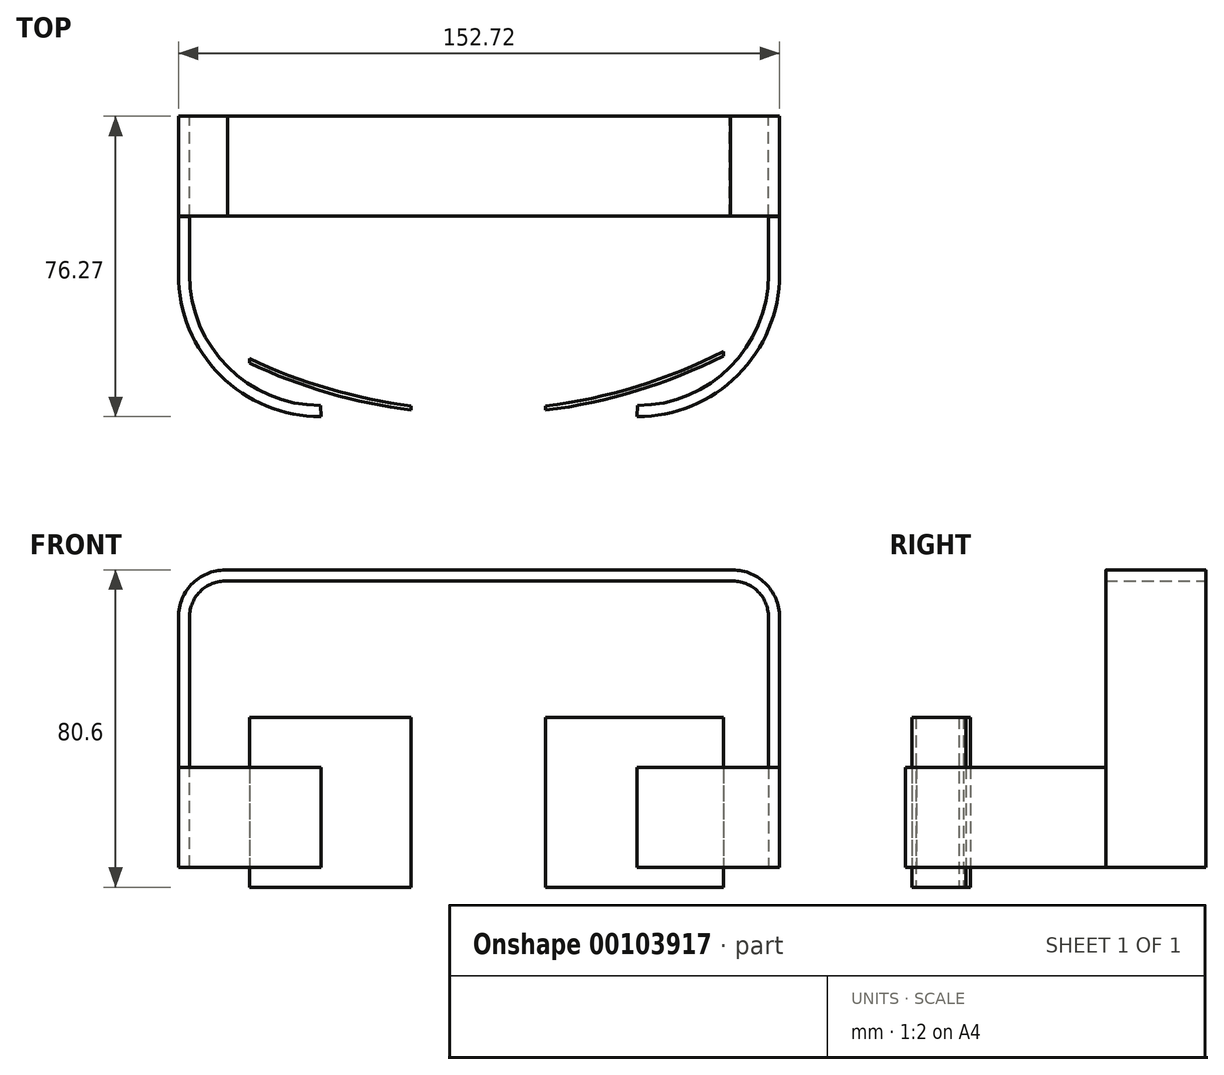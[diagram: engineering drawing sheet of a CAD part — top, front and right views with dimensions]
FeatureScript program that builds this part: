
annotation { "Feature Type Name" : "Feature", "Feature Type Description" : "" }
export const myFeature = defineFeature(function(context is Context, id is Id, definition is map)
    precondition{}
    {
        {
            var Q0;
            Q0=qCreatedBy(makeId("Front.planeOp"),FACE);
            var sketch = newSketch(context, id + "F0", { "sketchPlane" : qUnion([Q0])});
            skLineSegment(sketch, "E0", {"start": v(-76.36, 0) * mm, "end": v(-76.36, 63.57) * mm});
            skArc(sketch, "E1", {"start": v(-63.85, 75.5) * mm, "mid": v(-72.66, 72.22) * mm, "end": v(-76.36, 63.57) * mm});
            skLineSegment(sketch, "E2", {"start": v(-63.85, 75.5) * mm, "end": v(63.85, 75.5) * mm});
            skLineSegment(sketch, "E3", {"start": v(76.36, 0) * mm, "end": v(76.36, 63.57) * mm});
            skArc(sketch, "E4", {"start": v(76.36, 63.57) * mm, "mid": v(72.66, 72.22) * mm, "end": v(63.85, 75.5) * mm});
            skLineSegment(sketch, "E5", {"start": v(-73.55, 0) * mm, "end": v(-73.55, 63.57) * mm});
            skArc(sketch, "E6", {"start": v(-73.55, 63.57) * mm, "mid": v(-70.57, 70.32) * mm, "end": v(-63.58, 72.68) * mm});
            skLineSegment(sketch, "E7", {"start": v(-63.58, 72.68) * mm, "end": v(63.58, 72.68) * mm});
            skLineSegment(sketch, "E8", {"start": v(73.55, 0) * mm, "end": v(73.55, 63.57) * mm});
            skArc(sketch, "E9", {"start": v(73.55, 63.57) * mm, "mid": v(70.57, 70.32) * mm, "end": v(63.58, 72.68) * mm});
            skLineSegment(sketch, "E10", {"start": v(-76.36, 0) * mm, "end": v(-73.55, 0) * mm});
            skLineSegment(sketch, "E11", {"start": v(73.55, 0) * mm, "end": v(76.36, 0) * mm});
            skSolve(sketch);
        }
        {
            var Q0;
            Q0=qCreatedBy(makeId("Top.planeOp"),FACE);
            var sketch = newSketch(context, id + "F1", { "sketchPlane" : qUnion([Q0])});
            skLineSegment(sketch, "E12", {"start": v(73.55, -25.42) * mm, "end": v(73.55, -40.22) * mm});
            skLineSegment(sketch, "E13", {"start": v(76.36, -25.42) * mm, "end": v(76.36, -40.22) * mm});
            skLineSegment(sketch, "E14", {"start": v(-76.36, -25.42) * mm, "end": v(-76.36, -40.22) * mm});
            skLineSegment(sketch, "E15", {"start": v(-73.55, -25.42) * mm, "end": v(-73.55, -40.22) * mm});
            skArc(sketch, "E16", {"start": v(-73.55, -40.22) * mm, "mid": v(-63.81, -63.73) * mm, "end": v(-40.3, -73.46) * mm});
            skArc(sketch, "E17", {"start": v(-76.36, -40.22) * mm, "mid": v(-65.76, -65.75) * mm, "end": v(-40.2, -76.27) * mm});
            skArc(sketch, "E18", {"start": v(76.36, -40.22) * mm, "mid": v(65.76, -65.75) * mm, "end": v(40.2, -76.27) * mm});
            skArc(sketch, "E19", {"start": v(73.55, -40.22) * mm, "mid": v(63.81, -63.73) * mm, "end": v(40.3, -73.46) * mm});
            skLineSegment(sketch, "E20", {"start": v(-73.55, -25.42) * mm, "end": v(-76.36, -25.42) * mm});
            skLineSegment(sketch, "E21", {"start": v(-40.3, -73.46) * mm, "end": v(-40.2, -76.27) * mm});
            skLineSegment(sketch, "E22", {"start": v(40.2, -76.27) * mm, "end": v(40.3, -73.46) * mm});
            skLineSegment(sketch, "E23", {"start": v(73.55, -25.42) * mm, "end": v(76.36, -25.42) * mm});
            skSolve(sketch);
        }
        {
            var Q0;
            Q0 = qSketchRegion(id + "F0", true);
            extrude(context, id + "F2", {"entities" : qUnion([Q0]), "depth" : 25.4 * mm});
        }
        {
            var Q0;
            Q0=makeQuery(id+"F1.imprint","IMPRINT",FACE,{"disambiguationData":[TD([[makeQuery(id+"F1.imprint","IMPRINT",EDGE,{"derivedFrom":sQuery(id+"F1.wireOp",EDGE,"E12")}),1.0]])]});
            var Q1;
            Q1=makeQuery(id+"F1.imprint","IMPRINT",FACE,{"disambiguationData":[TD([[makeQuery(id+"F1.imprint","IMPRINT",EDGE,{"derivedFrom":sQuery(id+"F1.wireOp",EDGE,"E14")}),1.0]])]});
            var Q2;
            Q2=sQuery(id+"F1.wireOp",EDGE,"E20");
            var Q3;
            Q3=sQuery(id+"F1.wireOp",EDGE,"E15");
            var Q4;
            Q4=sQuery(id+"F1.wireOp",EDGE,"E14");
            var Q5;
            Q5=sQuery(id+"F1.wireOp",EDGE,"E17");
            var Q6;
            Q6=sQuery(id+"F1.wireOp",EDGE,"E16");
            var Q7;
            Q7=sQuery(id+"F1.wireOp",EDGE,"E21");
            var Q8;
            Q8=sQuery(id+"F1.wireOp",EDGE,"E12");
            var Q9;
            Q9=sQuery(id+"F1.wireOp",EDGE,"E13");
            var Q10;
            Q10=sQuery(id+"F1.wireOp",EDGE,"E23");
            var Q11;
            Q11=sQuery(id+"F1.wireOp",EDGE,"E18");
            var Q12;
            Q12=sQuery(id+"F1.wireOp",EDGE,"E19");
            var Q13;
            Q13=sQuery(id+"F1.wireOp",EDGE,"E22");
            extrude(context, id + "F3", {"entities" : qUnion([Q0, Q1]), "operationType" : NewBodyOperationType.ADD, "surfaceEntities" : qUnion([Q2, Q3, Q4, Q5, Q6, Q7, Q8, Q9, Q10, Q11, Q12, Q13]), "depth" : 25.4 * mm});
        }
        {
            var Q0;
            Q0=qCreatedBy(makeId("Top.planeOp"),FACE);
            var sketch = newSketch(context, id + "F4", { "sketchPlane" : qUnion([Q0])});
            skArc(sketch, "E24", {"start": v(-58.28, -62.73) * mm, "mid": v(-38.21, -70.3) * mm, "end": v(-17.21, -74.63) * mm});
            skArc(sketch, "E25", {"start": v(16.92, -74.67) * mm, "mid": v(40.1, -69.73) * mm, "end": v(62.1, -60.87) * mm});
            skArc(sketch, "E26", {"start": v(-58.28, -61.6) * mm, "mid": v(-38.22, -69.22) * mm, "end": v(-17.21, -73.6) * mm});
            skArc(sketch, "E27", {"start": v(16.92, -73.64) * mm, "mid": v(40.12, -68.65) * mm, "end": v(62.1, -59.72) * mm});
            skLineSegment(sketch, "E28", {"start": v(-58.28, -61.6) * mm, "end": v(-58.28, -62.73) * mm});
            skLineSegment(sketch, "E29", {"start": v(-17.21, -73.6) * mm, "end": v(-17.21, -74.63) * mm});
            skLineSegment(sketch, "E30", {"start": v(16.92, -74.67) * mm, "end": v(16.92, -73.64) * mm});
            skLineSegment(sketch, "E31", {"start": v(62.1, -59.72) * mm, "end": v(62.1, -60.87) * mm});
            skSolve(sketch);
        }
        {
            var Q0;
            Q0=makeQuery(id+"F4.imprint","IMPRINT",FACE,{"disambiguationData":[TD([[makeQuery(id+"F4.imprint","IMPRINT",EDGE,{"derivedFrom":sQuery(id+"F4.wireOp",EDGE,"E25")}),1.0]])]});
            var Q1;
            Q1=makeQuery(id+"F4.imprint","IMPRINT",FACE,{"disambiguationData":[TD([[makeQuery(id+"F4.imprint","IMPRINT",EDGE,{"derivedFrom":sQuery(id+"F4.wireOp",EDGE,"E24")}),1.0]])]});
            var Q2;
            Q2=sQuery(id+"F4.wireOp",EDGE,"E28");
            var Q3;
            Q3=sQuery(id+"F4.wireOp",EDGE,"E24");
            var Q4;
            Q4=sQuery(id+"F4.wireOp",EDGE,"E26");
            var Q5;
            Q5=sQuery(id+"F4.wireOp",EDGE,"E29");
            var Q6;
            Q6=sQuery(id+"F4.wireOp",EDGE,"E30");
            var Q7;
            Q7=sQuery(id+"F4.wireOp",EDGE,"E25");
            var Q8;
            Q8=sQuery(id+"F4.wireOp",EDGE,"E27");
            var Q9;
            Q9=sQuery(id+"F4.wireOp",EDGE,"E31");
            extrude(context, id + "F5", {"entities" : qUnion([Q0, Q1]), "surfaceEntities" : qUnion([Q2, Q3, Q4, Q5, Q6, Q7, Q8, Q9]), "depth" : 38.1 * mm, "hasSecondDirection" : true, "secondDirectionOppositeDirection" : true, "secondDirectionDepth" : 5.08 * mm});
        }
    });
